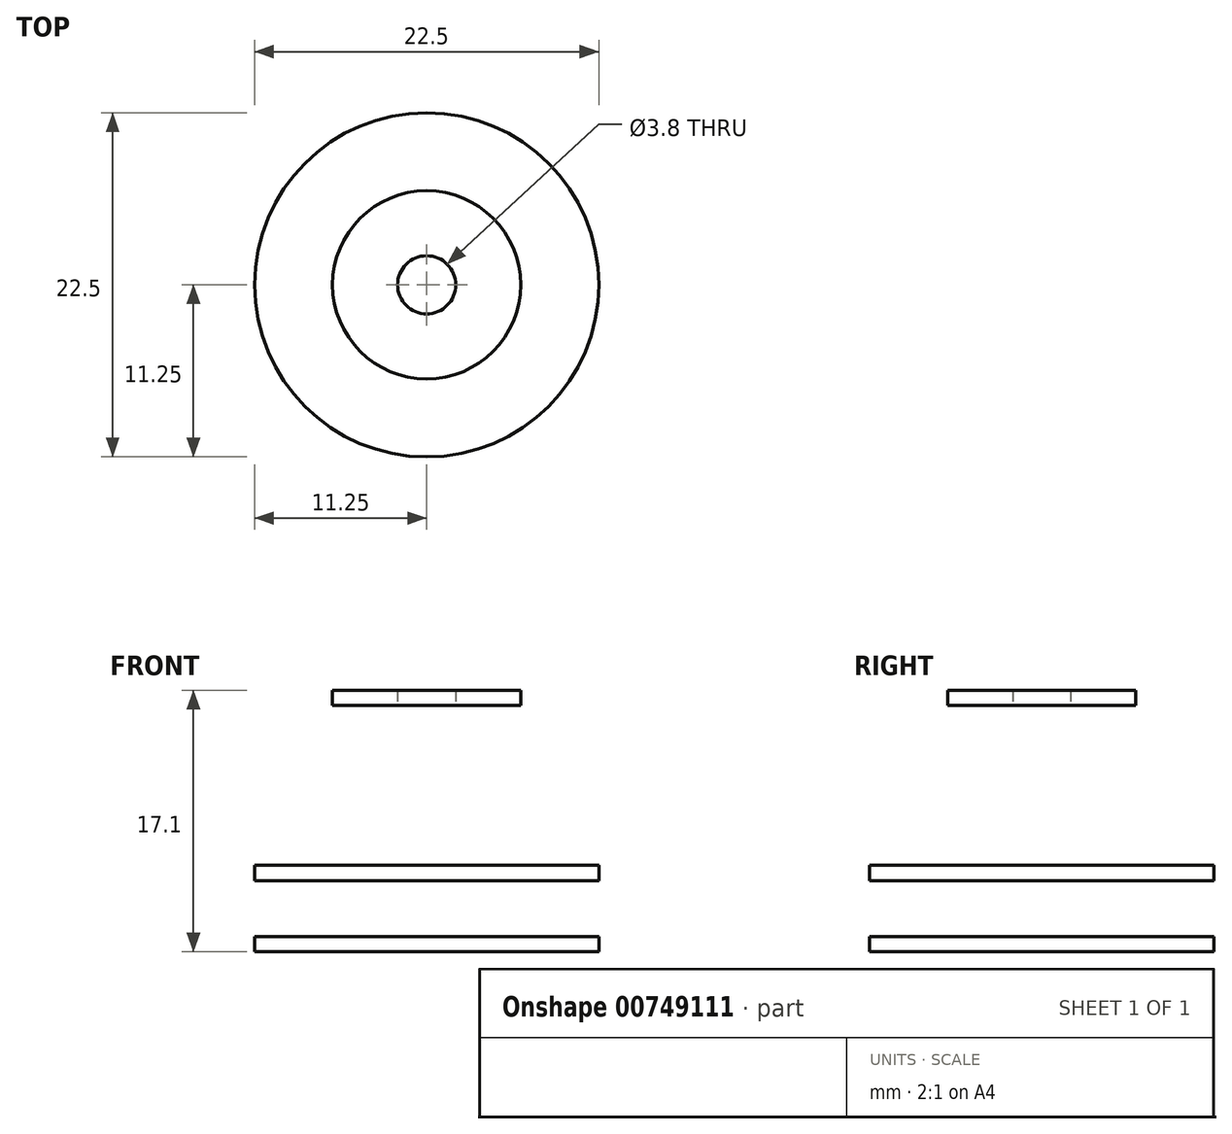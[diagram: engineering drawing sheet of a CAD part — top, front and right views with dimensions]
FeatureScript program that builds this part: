
annotation { "Feature Type Name" : "Feature", "Feature Type Description" : "" }
export const myFeature = defineFeature(function(context is Context, id is Id, definition is map)
    precondition{}
    {
        {
            var Q0;
            Q0=qCreatedBy(makeId("Top.planeOp"),FACE);
            var sketch = newSketch(context, id + "F0", { "sketchPlane" : qUnion([Q0])});
            skCircle(sketch, "E0", {"center": v(0, 0) * mm, "radius": 11.25 * mm});
            skSolve(sketch);
        }
        {
            var Q0;
            Q0=makeQuery(id+"F0.imprint","IMPRINT",FACE,{"disambiguationData":[TD([[makeQuery(id+"F0.imprint","IMPRINT",EDGE,{"derivedFrom":sQuery(id+"F0.wireOp",EDGE,"E0")}),1.0]])]});
            extrude(context, id + "F1", {"entities" : qUnion([Q0]), "depth" : 1 * mm, "offsetDistance" : 25 * mm});
        }
        {
            var Q0;
            Q0=makeQuery(id+"F1.opExtrude","CAP_FACE",FACE,{"disambiguationData":[OSD([sQuery(id+"F0.wireOp",EDGE,"E0")])],"isStart":false});
            cPlane(context, id + "F2", {"entities" : qUnion([Q0]), "cplaneType" : CPlaneType.OFFSET, "offset" : 3.65 * mm, "width" : 150 * mm, "height" : 150 * mm});
        }
        {
            var Q0;
            Q0=qCreatedBy(id+"F2.planeOp",FACE);
            var sketch = newSketch(context, id + "F3", { "sketchPlane" : qUnion([Q0])});
            skCircle(sketch, "E1", {"center": v(0, 0) * mm, "radius": 11.25 * mm});
            skSolve(sketch);
        }
        {
            var Q0;
            Q0=makeQuery(id+"F3.imprint","IMPRINT",FACE,{"disambiguationData":[TD([[makeQuery(id+"F3.imprint","IMPRINT",EDGE,{"derivedFrom":sQuery(id+"F3.wireOp",EDGE,"E1")}),1.0]])]});
            extrude(context, id + "F4", {"entities" : qUnion([Q0]), "depth" : 1 * mm, "offsetDistance" : 25 * mm});
        }
        {
            var Q0;
            Q0=makeQuery(id+"F4.opExtrude","CAP_FACE",FACE,{"disambiguationData":[OSD([sQuery(id+"F3.wireOp",EDGE,"E1")])],"isStart":false});
            cPlane(context, id + "F5", {"entities" : qUnion([Q0]), "cplaneType" : CPlaneType.OFFSET, "offset" : 10.45 * mm, "width" : 150 * mm, "height" : 150 * mm});
        }
        {
            var Q0;
            Q0=qCreatedBy(id+"F5.planeOp",FACE);
            var sketch = newSketch(context, id + "F6", { "sketchPlane" : qUnion([Q0])});
            skCircle(sketch, "E2", {"center": v(0, 0) * mm, "radius": 6.15 * mm});
            skCircle(sketch, "E3", {"center": v(0, 0) * mm, "radius": 1.9 * mm});
            skSolve(sketch);
        }
        {
            var Q0;
            Q0 = qSketchRegion(id + "F6", true);
            extrude(context, id + "F7", {"entities" : qUnion([Q0]), "depth" : 1 * mm, "offsetDistance" : 25 * mm});
        }
    });
